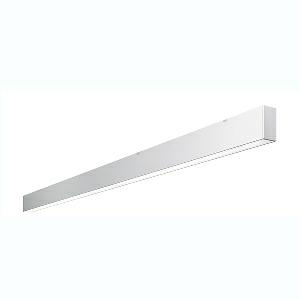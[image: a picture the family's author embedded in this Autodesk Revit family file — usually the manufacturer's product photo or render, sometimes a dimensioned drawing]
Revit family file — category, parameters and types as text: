
# Revit family: dotoo_line_-_dla_3000_830_d_end_00807948_7158
name_source: partatom
category: Lighting Fixtures
units: mm (PartAtom-declared; Revit-internal decimal feet)

## family parameters
Cut with Voids When Loaded = No
Host = Face
Light Source = No
Part Type = Normal
Room Calculation Point = No
Round Connector Dimension = Use Diameter
Shared = No

## types (1)
- DOTOO.line - DLA 3000/830/D END (1 x LED, 2650 lm, 3000K)
    Apparent Load = 26 VA
    Approval mark = CE
    CIE Flux Codes = 67 91 98 100 100
    Color Rendering = 80-89
    Color Temperature = 3000K
    Control Gear = Electronic ballast
    Default Elevation = 1800 mm
    Description = DLA 3000/830/D|Surface-mounted luminaire.|light source: LED|work equipment: Adjustable electronic ballast, digital DALI|connected load: 220-240 V, 50/60 Hz|Power consumption: approx. 26 W|luminous flux: 2650 lm|luminous efficacy: 101 lm/W|light distribution: Direct|colour temperature: Warm white, ca. 3000 K|class of protection: I|technology: Continuously dimmable|mains lead: Connector|glare control: Prism aperture|special features: DALI Load 1x, TouchDIM - dimming via standard switch, Through-wired, up to 18 m on one mains connection, Flicker-free, Suitable as emergency lighting, Mechanical and electrical connection of the individual modules without tools|
    Frequency = 50 Hz
    Height = 110 mm
    Lamp = 1 x LED
    Lamp Light Flux = 2650 lm
    Lamp count = 1
    Length = 2250 mm
    Luminous efficacy = 102 lm/W
    Manufacturer = Waldmann
    ModVariant = No
    Model = 00807948
    Mounting Place = Ceiling
    Mounting Type = Surface mounted
    Number of Poles = 1
    OnlyDefault = Yes
    Power Factor = 1
    Product Name = DOTOO.line - DLA 3000/830/D END
    Product group = Ceiling mounted luminaire
    ProductGroupID = 3
    Protection Class = Protection class I
    Protection Degree = IP 40
    RLX_Detail_Level = 1
    RLX_Emergency_Light_Flux = 0 lm
    RLX_Emergency_Type = 0
    RLX_Emergency_Type_DB = No
    RlxData = <blob elided: 19385 chars, md5=02013fe0>
    Socket = socket
    Standby Power = 0 W
    System Light Flux = 2650 lm
    System Power = 26 W
    Type Comments = Product without accessories
    Type Image = 114359000-00807936.jpg
    URL = http://relux.com
    VarID = ---
    Voltage = 230 V
    Voltage Range = 220-240 V
    Weight = 0.00 kg
    Width = 60 mm  [stored 0.19685 ft]

note: [stored X ft] marks values corroborated as IEEE doubles in the binary element streams (Revit-internal decimal feet)

## geometry (parser evidence)
native form markers: Blend x4, Sweep x12
no freeform markers — native parametric forms only
